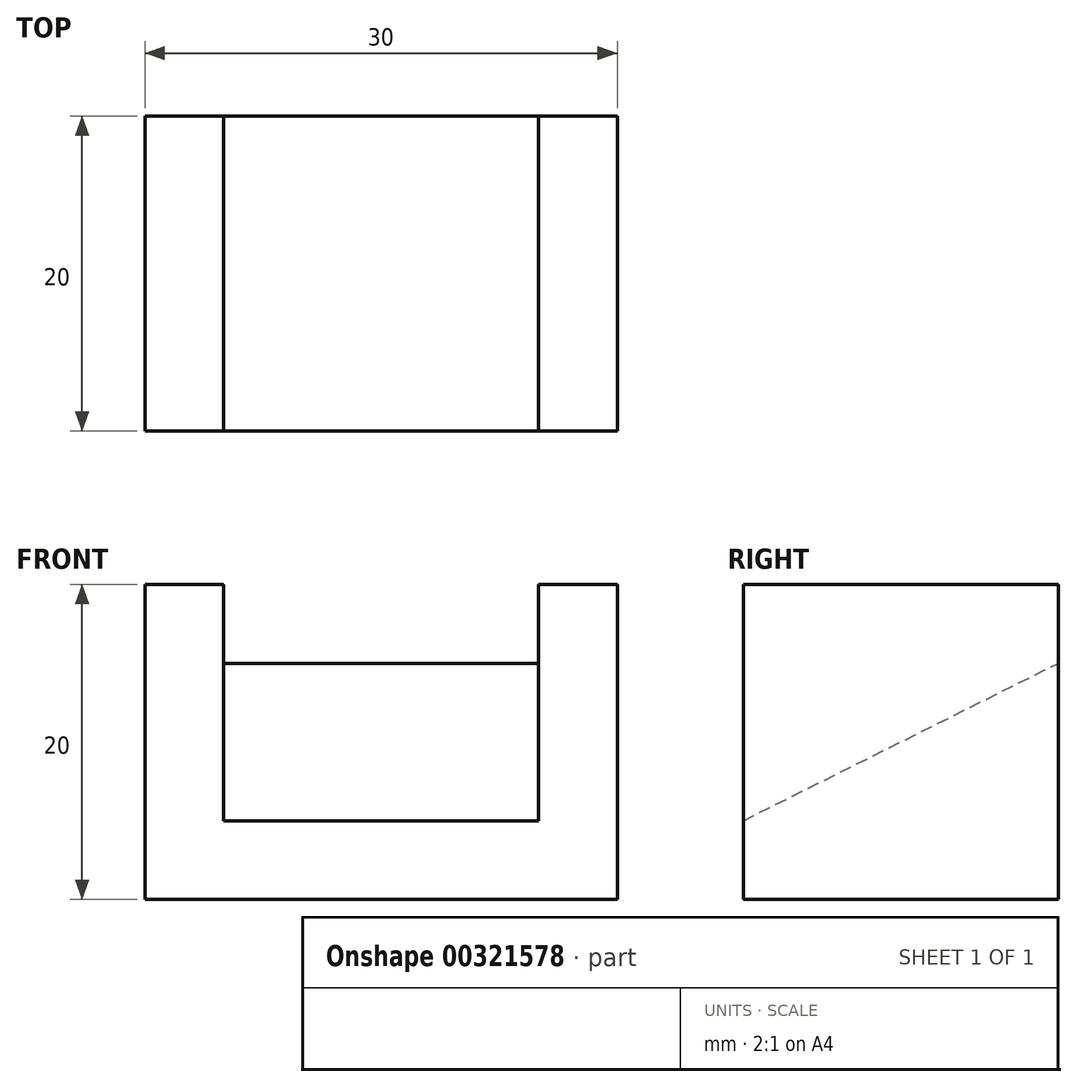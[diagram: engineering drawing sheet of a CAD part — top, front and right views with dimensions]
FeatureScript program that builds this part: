
annotation { "Feature Type Name" : "Feature", "Feature Type Description" : "" }
export const myFeature = defineFeature(function(context is Context, id is Id, definition is map)
    precondition{}
    {
        {
            var Q0;
            Q0=qCreatedBy(makeId("Front.planeOp"),FACE);
            var sketch = newSketch(context, id + "F0", { "sketchPlane" : qUnion([Q0])});
            skLineSegment(sketch, "E0", {"start": v(0, 0) * mm, "end": v(0, 20) * mm});
            skLineSegment(sketch, "E1", {"start": v(0, 20) * mm, "end": v(5, 20) * mm});
            skLineSegment(sketch, "E2", {"start": v(5, 20) * mm, "end": v(5, 5) * mm});
            skLineSegment(sketch, "E3", {"start": v(5, 5) * mm, "end": v(25, 5) * mm});
            skLineSegment(sketch, "E4", {"start": v(25, 5) * mm, "end": v(25, 20) * mm});
            skLineSegment(sketch, "E5", {"start": v(25, 20) * mm, "end": v(30, 20) * mm});
            skLineSegment(sketch, "E6", {"start": v(30, 20) * mm, "end": v(30, 0) * mm});
            skLineSegment(sketch, "E7", {"start": v(30, 0) * mm, "end": v(0, 0) * mm});
            skSolve(sketch);
        }
        {
            var Q0;
            Q0 = qSketchRegion(id + "F0", true);
            extrude(context, id + "F1", {"entities" : qUnion([Q0]), "depth" : 20 * mm});
        }
        {
            var Q0;
            Q0=makeQuery(id+"F1.opExtrude","SWEPT_FACE",FACE,{"disambiguationData":[OSD([sQuery(id+"F0.wireOp",EDGE,"E6")])]});
            var sketch = newSketch(context, id + "F2", { "sketchPlane" : qUnion([Q0])});
            skLineSegment(sketch, "E8", {"start": v(0, 15) * mm, "end": v(-20, 5) * mm});
            skLineSegment(sketch, "E9", {"start": v(-20, 5) * mm, "end": v(-20, 0) * mm});
            skLineSegment(sketch, "E10", {"start": v(-20, 0) * mm, "end": v(0, 0) * mm});
            skLineSegment(sketch, "E11", {"start": v(0, 0) * mm, "end": v(0, 15) * mm});
            skSolve(sketch);
        }
        {
            var Q0;
            Q0 = qSketchRegion(id + "F2", true);
            extrude(context, id + "F3", {"entities" : qUnion([Q0]), "operationType" : NewBodyOperationType.ADD, "oppositeDirection" : true, "depth" : 25.5 * mm});
        }
    });
